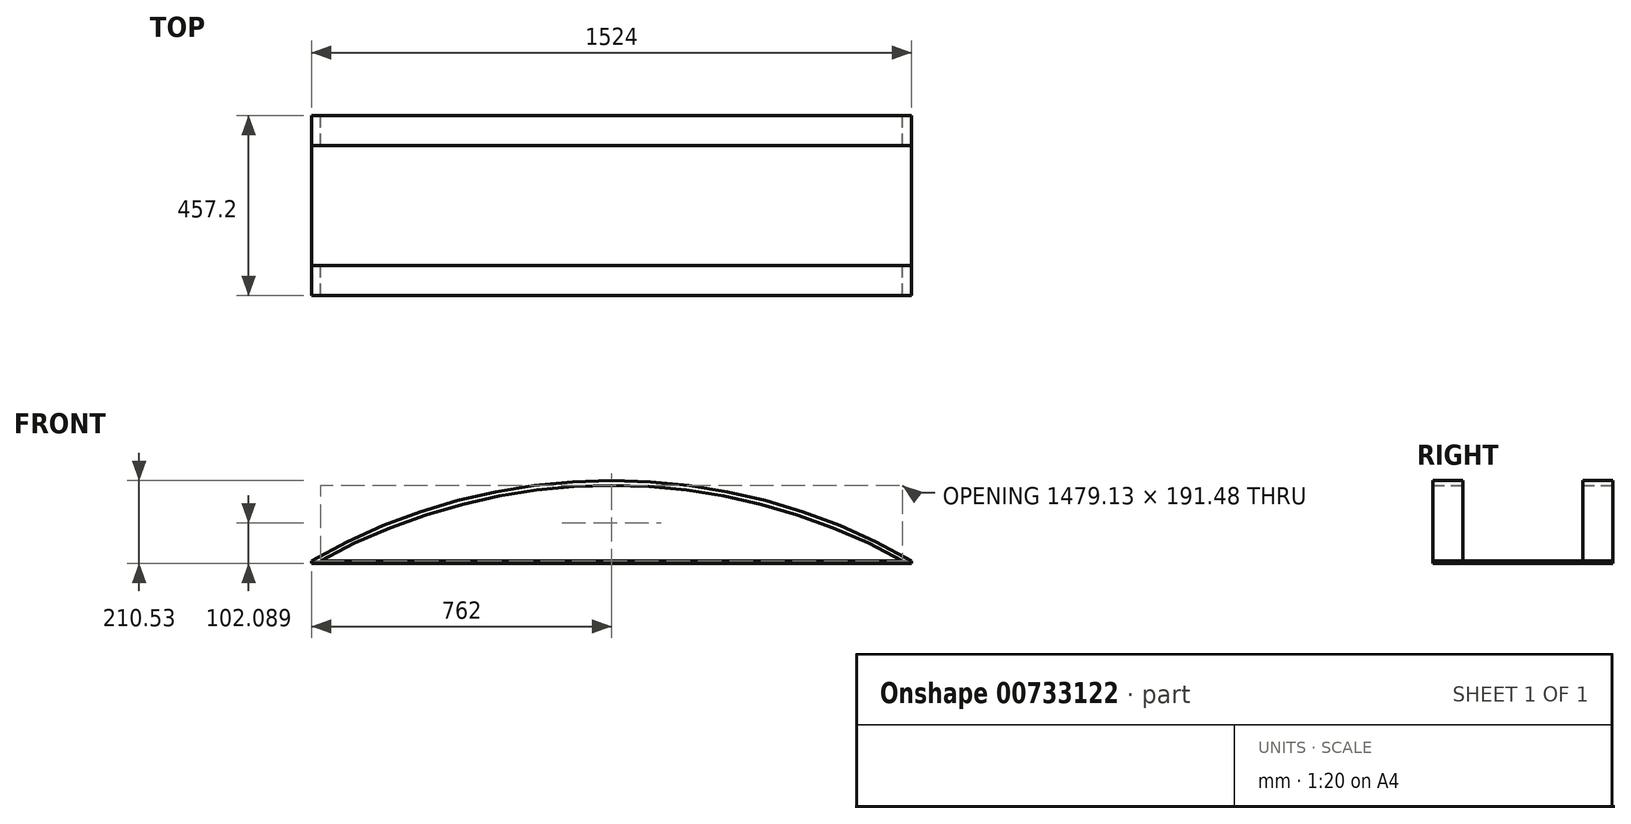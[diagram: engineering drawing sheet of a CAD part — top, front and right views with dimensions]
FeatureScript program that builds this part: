
annotation { "Feature Type Name" : "Feature", "Feature Type Description" : "" }
export const myFeature = defineFeature(function(context is Context, id is Id, definition is map)
    precondition{}
    {
        {
            var Q0;
            Q0=qCreatedBy(makeId("Front.planeOp"),FACE);
            var sketch = newSketch(context, id + "F0", { "sketchPlane" : qUnion([Q0])});
            skArc(sketch, "E0", {"start": v(762, 0) * mm, "mid": v(0, 204.18) * mm, "end": v(-762, 0) * mm});
            skLineSegment(sketch, "E1", {"start": v(0, 0) * mm, "end": v(0, -1319.82) * mm, "construction": true});
            skLineSegment(sketch, "E2", {"start": v(0, 0) * mm, "end": v(-762, 0) * mm, "construction": true});
            skLineSegment(sketch, "E3", {"start": v(0, 0) * mm, "end": v(762, 0) * mm, "construction": true});
            skLineSegment(sketch, "E4", {"start": v(-762, 0) * mm, "end": v(-739.57, 0) * mm});
            skLineSegment(sketch, "E5", {"start": v(762, 0) * mm, "end": v(739.57, 0) * mm});
            skArc(sketch, "E6", {"start": v(739.57, 0) * mm, "mid": v(0, 191.48) * mm, "end": v(-739.57, 0) * mm});
            skSolve(sketch);
        }
        {
            var Q0;
            Q0 = qSketchRegion(id + "F0", true);
            extrude(context, id + "F1", {"entities" : qUnion([Q0]), "endBound" : BoundingType.SYMMETRIC, "depth" : 457.2 * mm, "offsetDistance" : 25.4 * mm});
        }
        {
            var Q0;
            Q0 = qSketchRegion(id + "F0", true);
            extrude(context, id + "F2", {"entities" : qUnion([Q0]), "operationType" : NewBodyOperationType.REMOVE, "endBound" : BoundingType.SYMMETRIC, "oppositeDirection" : true, "depth" : 304.8 * mm, "offsetDistance" : 25.4 * mm});
        }
        {
            var Q0;
            Q0=qCreatedBy(makeId("Right.planeOp"),FACE);
            var sketch = newSketch(context, id + "F3", { "sketchPlane" : qUnion([Q0])});
            skLineSegment(sketch, "E7.bottom", {"start": v(-228.6, 0) * mm, "end": v(228.6, 0) * mm});
            skLineSegment(sketch, "E7.top", {"start": v(-228.6, -6.35) * mm, "end": v(228.6, -6.35) * mm});
            skLineSegment(sketch, "E7.left", {"start": v(-228.6, 0) * mm, "end": v(-228.6, -6.35) * mm});
            skLineSegment(sketch, "E7.right", {"start": v(228.6, 0) * mm, "end": v(228.6, -6.35) * mm});
            skSolve(sketch);
        }
        {
            var Q0;
            Q0 = qSketchRegion(id + "F3", true);
            extrude(context, id + "F4", {"entities" : qUnion([Q0]), "operationType" : NewBodyOperationType.ADD, "endBound" : BoundingType.SYMMETRIC, "depth" : 1524 * mm, "offsetDistance" : 25.4 * mm});
        }
    });
